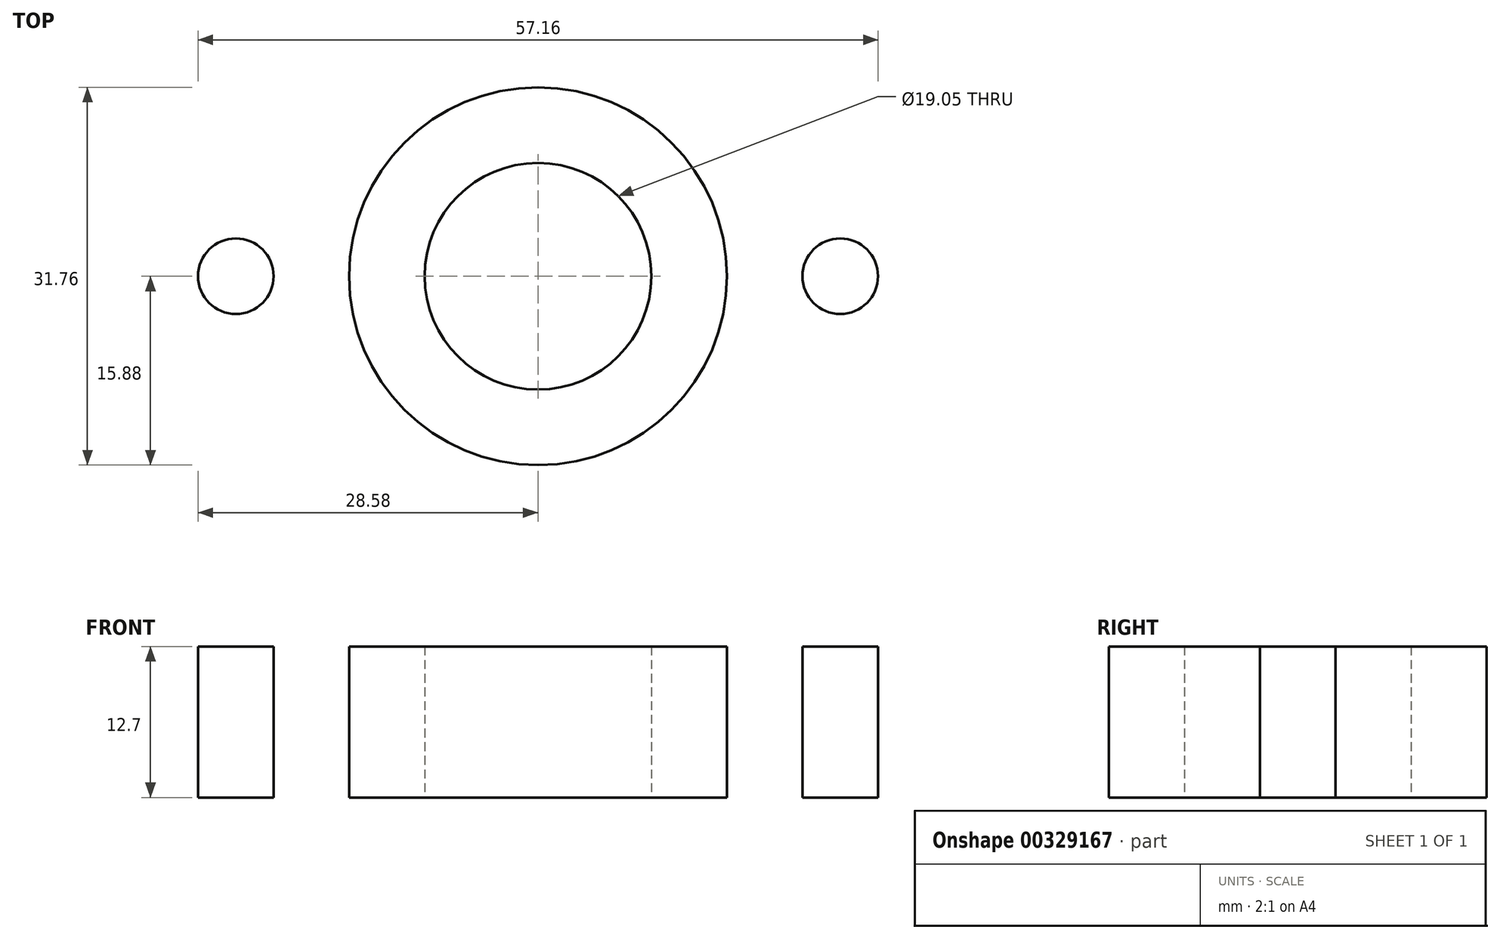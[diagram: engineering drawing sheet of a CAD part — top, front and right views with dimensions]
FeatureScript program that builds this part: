
annotation { "Feature Type Name" : "Feature", "Feature Type Description" : "" }
export const myFeature = defineFeature(function(context is Context, id is Id, definition is map)
    precondition{}
    {
        {
            var Q0;
            Q0=qCreatedBy(makeId("Front.planeOp"),FACE);
            var sketch = newSketch(context, id + "F0", { "sketchPlane" : qUnion([Q0])});
            skLineSegment(sketch, "E0.bottom", {"start": v(0, 0) * mm, "end": v(63.5, 0) * mm});
            skLineSegment(sketch, "E0.top", {"start": v(0, 12.7) * mm, "end": v(63.5, 12.7) * mm});
            skLineSegment(sketch, "E0.left", {"start": v(0, 0) * mm, "end": v(0, 12.7) * mm});
            skLineSegment(sketch, "E0.right", {"start": v(63.5, 0) * mm, "end": v(63.5, 12.7) * mm});
            skLineSegment(sketch, "E1.bottom", {"start": v(15.87, 12.7) * mm, "end": v(47.62, 12.7) * mm});
            skLineSegment(sketch, "E1.top", {"start": v(15.87, 25.4) * mm, "end": v(47.62, 25.4) * mm});
            skLineSegment(sketch, "E1.left", {"start": v(15.87, 12.7) * mm, "end": v(15.87, 25.4) * mm});
            skLineSegment(sketch, "E1.right", {"start": v(47.62, 12.7) * mm, "end": v(47.62, 25.4) * mm});
            skLineSegment(sketch, "E2", {"start": v(31.75, 25.4) * mm, "end": v(31.75, 0) * mm, "construction": true});
            skSolve(sketch);
        }
        {
            var Q0;
            Q0=makeQuery(id+"F0.imprint","IMPRINT",FACE,{"disambiguationData":[TD([[makeQuery(id+"F0.imprint","IMPRINT",EDGE,{"derivedFrom":sQuery(id+"F0.wireOp",EDGE,"E0.bottom")}),1.0]])]});
            var Q1;
            Q1=makeQuery(id+"F0.imprint","IMPRINT",FACE,{"disambiguationData":[TD([[makeQuery(id+"F0.imprint","IMPRINT",EDGE,{"derivedFrom":sQuery(id+"F0.wireOp",EDGE,"E1.bottom")}),1.0]])]});
            extrude(context, id + "F1", {"entities" : qUnion([Q0, Q1]), "depth" : 63.5 * mm});
        }
        {
            var Q0;
            Q0=makeQuery(id+"F1.opExtrude","SWEPT_FACE",FACE,{"disambiguationData":[OSD([sQuery(id+"F0.wireOp",EDGE,"E0.bottom")])]});
            var sketch = newSketch(context, id + "F2", { "sketchPlane" : qUnion([Q0])});
            skCircle(sketch, "E3", {"center": v(31.75, 31.75) * mm, "radius": 9.52 * mm});
            skPoint(sketch, "E3.centerSnap0", {"position": v(0, 31.75) * mm});
            skPoint(sketch, "E3.centerSnap1", {"position": v(31.75, 63.5) * mm});
            skCircle(sketch, "E4", {"center": v(31.75, 31.75) * mm, "radius": 15.88 * mm});
            skCircle(sketch, "E5", {"center": v(31.75, 31.75) * mm, "radius": 25.4 * mm});
            skCircle(sketch, "E6", {"center": v(31.75, 31.75) * mm, "radius": 31.75 * mm});
            skCircle(sketch, "E7", {"center": v(31.75, 57.15) * mm, "radius": 3.18 * mm});
            skCircle(sketch, "E8", {"center": v(6.35, 31.75) * mm, "radius": 3.18 * mm});
            skCircle(sketch, "E9", {"center": v(31.75, 6.35) * mm, "radius": 3.18 * mm});
            skPoint(sketch, "E9.centerSnap0", {"position": v(31.75, 0) * mm});
            skCircle(sketch, "E10", {"center": v(57.15, 31.75) * mm, "radius": 3.18 * mm});
            skPoint(sketch, "E10.centerSnap0", {"position": v(63.5, 31.75) * mm});
            skSolve(sketch);
        }
        {
            var Q0;
            {var subQ0=sQuery(id+"F2.wireOp",EDGE,"E6");var subQ1=sQuery(id+"F0.wireOp",EDGE,"E0.bottom");var subQ2=makeQuery(id+"F1.opExtrude","CAP_EDGE",EDGE,{"disambiguationData":[OSD([subQ1])],"isStart":false});var subQ3=makeQuery(id+"F2.imprint","INTERSECT",VERTEX,{"derivedFrom":[subQ2,subQ0]});Q0=makeQuery(id+"F2.imprint","IMPRINT",FACE,{"disambiguationData":[TD([[makeQuery(id+"F2.imprint","IMPRINT",EDGE,{"disambiguationData":[TD([[subQ3,-1.0]])],"derivedFrom":subQ0}),-1.0]])]});}
            var Q1;
            {var subQ0=sQuery(id+"F2.wireOp",EDGE,"E6");var subQ1=sQuery(id+"F0.wireOp",EDGE,"E0.bottom");var subQ2=makeQuery(id+"F1.opExtrude","CAP_EDGE",EDGE,{"disambiguationData":[OSD([subQ1])],"isStart":false});var subQ3=makeQuery(id+"F2.imprint","INTERSECT",VERTEX,{"derivedFrom":[subQ2,subQ0]});Q1=makeQuery(id+"F2.imprint","IMPRINT",FACE,{"disambiguationData":[TD([[makeQuery(id+"F2.imprint","IMPRINT",EDGE,{"disambiguationData":[TD([[subQ3,1.0]])],"derivedFrom":subQ0}),-1.0]])]});}
            var Q2;
            {var subQ0=sQuery(id+"F2.wireOp",EDGE,"E6");var subQ1=sQuery(id+"F0.wireOp",EDGE,"E0.bottom");var subQ4=makeQuery(id+"F1.opExtrude","CAP_EDGE",EDGE,{"disambiguationData":[OSD([subQ1])],"isStart":true});var subQ5=makeQuery(id+"F2.imprint","INTERSECT",VERTEX,{"derivedFrom":[subQ4,subQ0]});Q2=makeQuery(id+"F2.imprint","IMPRINT",FACE,{"disambiguationData":[TD([[makeQuery(id+"F2.imprint","IMPRINT",EDGE,{"disambiguationData":[TD([[subQ5,1.0]])],"derivedFrom":subQ0}),-1.0]])]});}
            var Q3;
            {var subQ0=sQuery(id+"F2.wireOp",EDGE,"E6");var subQ1=sQuery(id+"F0.wireOp",EDGE,"E0.bottom");var subQ4=makeQuery(id+"F1.opExtrude","CAP_EDGE",EDGE,{"disambiguationData":[OSD([subQ1])],"isStart":true});var subQ5=makeQuery(id+"F2.imprint","INTERSECT",VERTEX,{"derivedFrom":[subQ4,subQ0]});Q3=makeQuery(id+"F2.imprint","IMPRINT",FACE,{"disambiguationData":[TD([[makeQuery(id+"F2.imprint","IMPRINT",EDGE,{"disambiguationData":[TD([[subQ5,-1.0]])],"derivedFrom":subQ0}),-1.0]])]});}
            extrude(context, id + "F3", {"entities" : qUnion([Q0, Q1, Q2, Q3]), "operationType" : NewBodyOperationType.REMOVE, "endBound" : BoundingType.THROUGH_ALL, "oppositeDirection" : true, "depth" : 25.4 * mm});
        }
        {
            var Q0;
            {var subQ0=sQuery(id+"F2.wireOp",EDGE,"E7");var subQ1=sQuery(id+"F2.wireOp",EDGE,"E5");var subQ2=makeQuery(id+"F2.imprint","INTERSECT",VERTEX,{"disambiguationData":[OD(0.0)],"derivedFrom":[subQ1,subQ0]});Q0=makeQuery(id+"F2.imprint","IMPRINT",FACE,{"disambiguationData":[TD([[makeQuery(id+"F2.imprint","IMPRINT",EDGE,{"disambiguationData":[TD([[subQ2,-1.0]])],"derivedFrom":subQ1}),-1.0]])]});}
            var Q1;
            {var subQ0=sQuery(id+"F2.wireOp",EDGE,"E7");var subQ1=sQuery(id+"F2.wireOp",EDGE,"E5");var subQ2=makeQuery(id+"F2.imprint","INTERSECT",VERTEX,{"disambiguationData":[OD(0.0)],"derivedFrom":[subQ1,subQ0]});Q1=makeQuery(id+"F2.imprint","IMPRINT",FACE,{"disambiguationData":[TD([[makeQuery(id+"F2.imprint","IMPRINT",EDGE,{"disambiguationData":[TD([[subQ2,-1.0]])],"derivedFrom":subQ1}),1.0]])]});}
            var Q2;
            {var subQ0=sQuery(id+"F2.wireOp",EDGE,"E8");var subQ1=sQuery(id+"F2.wireOp",EDGE,"E5");var subQ2=makeQuery(id+"F2.imprint","INTERSECT",VERTEX,{"disambiguationData":[OD(0.0)],"derivedFrom":[subQ1,subQ0]});Q2=makeQuery(id+"F2.imprint","IMPRINT",FACE,{"disambiguationData":[TD([[makeQuery(id+"F2.imprint","IMPRINT",EDGE,{"disambiguationData":[TD([[subQ2,-1.0]])],"derivedFrom":subQ1}),1.0]])]});}
            var Q3;
            {var subQ0=sQuery(id+"F2.wireOp",EDGE,"E8");var subQ1=sQuery(id+"F2.wireOp",EDGE,"E5");var subQ2=makeQuery(id+"F2.imprint","INTERSECT",VERTEX,{"disambiguationData":[OD(0.0)],"derivedFrom":[subQ1,subQ0]});Q3=makeQuery(id+"F2.imprint","IMPRINT",FACE,{"disambiguationData":[TD([[makeQuery(id+"F2.imprint","IMPRINT",EDGE,{"disambiguationData":[TD([[subQ2,-1.0]])],"derivedFrom":subQ1}),-1.0]])]});}
            var Q4;
            {var subQ0=sQuery(id+"F2.wireOp",EDGE,"E9");var subQ1=sQuery(id+"F2.wireOp",EDGE,"E5");var subQ2=makeQuery(id+"F2.imprint","INTERSECT",VERTEX,{"disambiguationData":[OD(0.0)],"derivedFrom":[subQ1,subQ0]});Q4=makeQuery(id+"F2.imprint","IMPRINT",FACE,{"disambiguationData":[TD([[makeQuery(id+"F2.imprint","IMPRINT",EDGE,{"disambiguationData":[TD([[subQ2,-1.0]])],"derivedFrom":subQ1}),-1.0]])]});}
            var Q5;
            {var subQ0=sQuery(id+"F2.wireOp",EDGE,"E9");var subQ1=sQuery(id+"F2.wireOp",EDGE,"E5");var subQ2=makeQuery(id+"F2.imprint","INTERSECT",VERTEX,{"disambiguationData":[OD(0.0)],"derivedFrom":[subQ1,subQ0]});Q5=makeQuery(id+"F2.imprint","IMPRINT",FACE,{"disambiguationData":[TD([[makeQuery(id+"F2.imprint","IMPRINT",EDGE,{"disambiguationData":[TD([[subQ2,-1.0]])],"derivedFrom":subQ1}),1.0]])]});}
            var Q6;
            {var subQ0=sQuery(id+"F2.wireOp",EDGE,"E10");var subQ1=sQuery(id+"F2.wireOp",EDGE,"E5");var subQ2=makeQuery(id+"F2.imprint","INTERSECT",VERTEX,{"disambiguationData":[OD(0.0)],"derivedFrom":[subQ1,subQ0]});Q6=makeQuery(id+"F2.imprint","IMPRINT",FACE,{"disambiguationData":[TD([[makeQuery(id+"F2.imprint","IMPRINT",EDGE,{"disambiguationData":[TD([[subQ2,1.0]])],"derivedFrom":subQ1}),-1.0]])]});}
            var Q7;
            {var subQ0=sQuery(id+"F2.wireOp",EDGE,"E10");var subQ1=sQuery(id+"F2.wireOp",EDGE,"E5");var subQ2=makeQuery(id+"F2.imprint","INTERSECT",VERTEX,{"disambiguationData":[OD(0.0)],"derivedFrom":[subQ1,subQ0]});Q7=makeQuery(id+"F2.imprint","IMPRINT",FACE,{"disambiguationData":[TD([[makeQuery(id+"F2.imprint","IMPRINT",EDGE,{"disambiguationData":[TD([[subQ2,1.0]])],"derivedFrom":subQ1}),1.0]])]});}
            var Q8;
            Q8=makeQuery(id+"F2.imprint","IMPRINT",FACE,{"disambiguationData":[TD([[makeQuery(id+"F2.imprint","IMPRINT",EDGE,{"derivedFrom":sQuery(id+"F2.wireOp",EDGE,"E3")}),1.0]])]});
            extrude(context, id + "F4", {"entities" : qUnion([Q0, Q1, Q2, Q3, Q4, Q5, Q6, Q7, Q8]), "operationType" : NewBodyOperationType.REMOVE, "endBound" : BoundingType.THROUGH_ALL, "oppositeDirection" : true, "depth" : 25.4 * mm});
        }
    });
